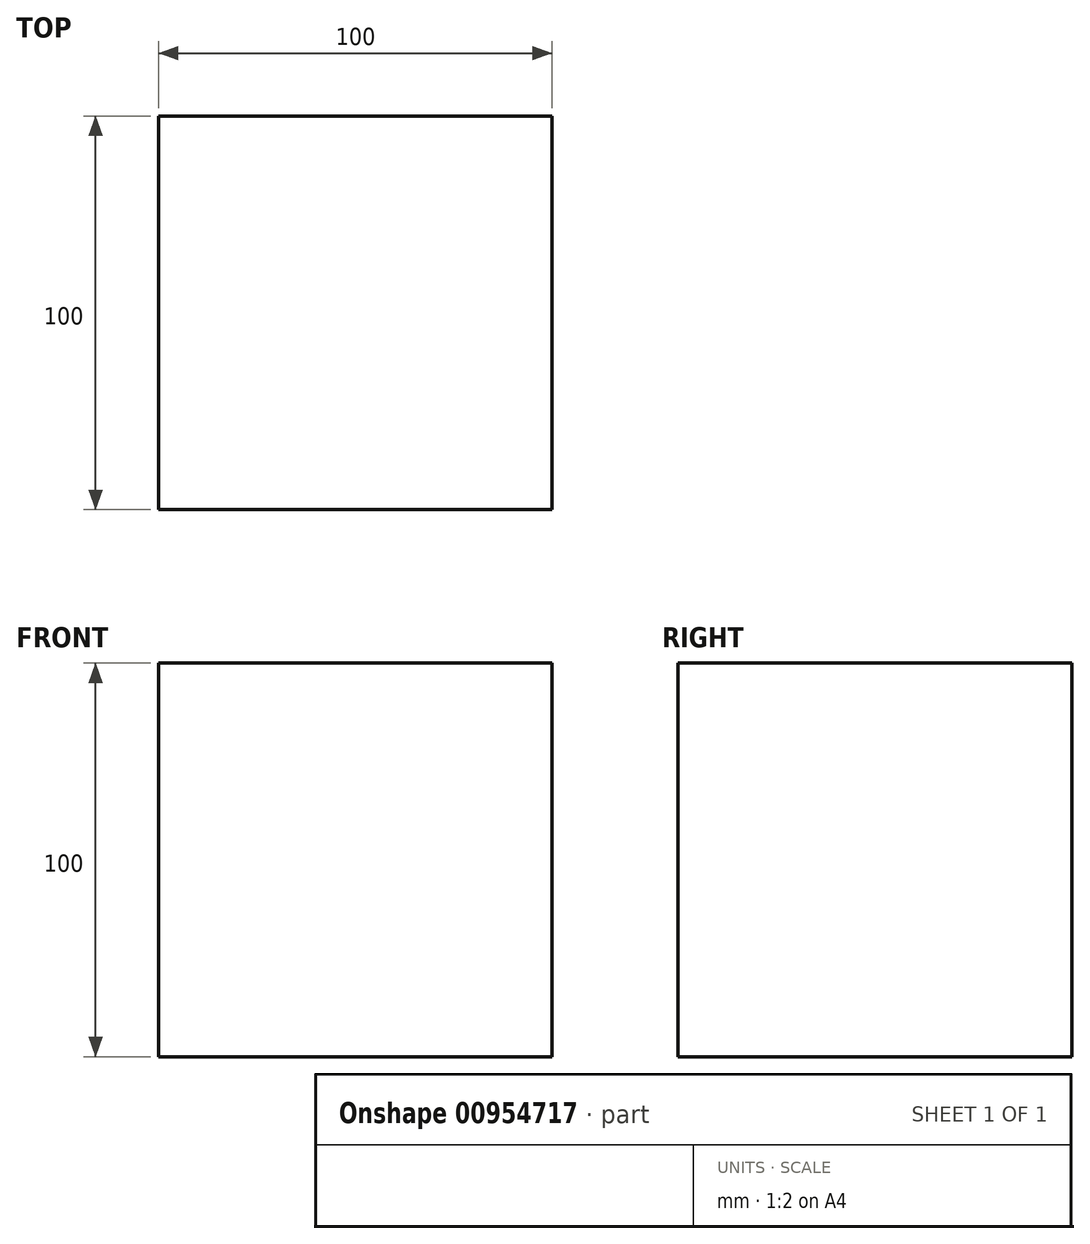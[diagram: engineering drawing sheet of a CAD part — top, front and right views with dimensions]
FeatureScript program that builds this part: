
annotation { "Feature Type Name" : "Feature", "Feature Type Description" : "" }
export const myFeature = defineFeature(function(context is Context, id is Id, definition is map)
    precondition{}
    {
        {
            var Q0;
            Q0=qCreatedBy(makeId("Top.planeOp"),FACE);
            var sketch = newSketch(context, id + "F0", { "sketchPlane" : qUnion([Q0])});
            skLineSegment(sketch, "E0.bottom", {"start": v(50, -54.06) * mm, "end": v(-50, -54.06) * mm});
            skLineSegment(sketch, "E0.top", {"start": v(50, 45.94) * mm, "end": v(-50, 45.94) * mm});
            skLineSegment(sketch, "E0.left", {"start": v(50, -54.06) * mm, "end": v(50, 45.94) * mm});
            skLineSegment(sketch, "E0.right", {"start": v(-50, -54.06) * mm, "end": v(-50, 45.94) * mm});
            skPoint(sketch, "E0.middle", {"position": v(0, -4.06) * mm});
            skSolve(sketch);
        }
        {
            var Q0;
            Q0 = qSketchRegion(id + "F0", true);
            extrude(context, id + "F1", {"entities" : qUnion([Q0]), "depth" : 100 * mm, "offsetDistance" : 25 * mm});
        }
    });
